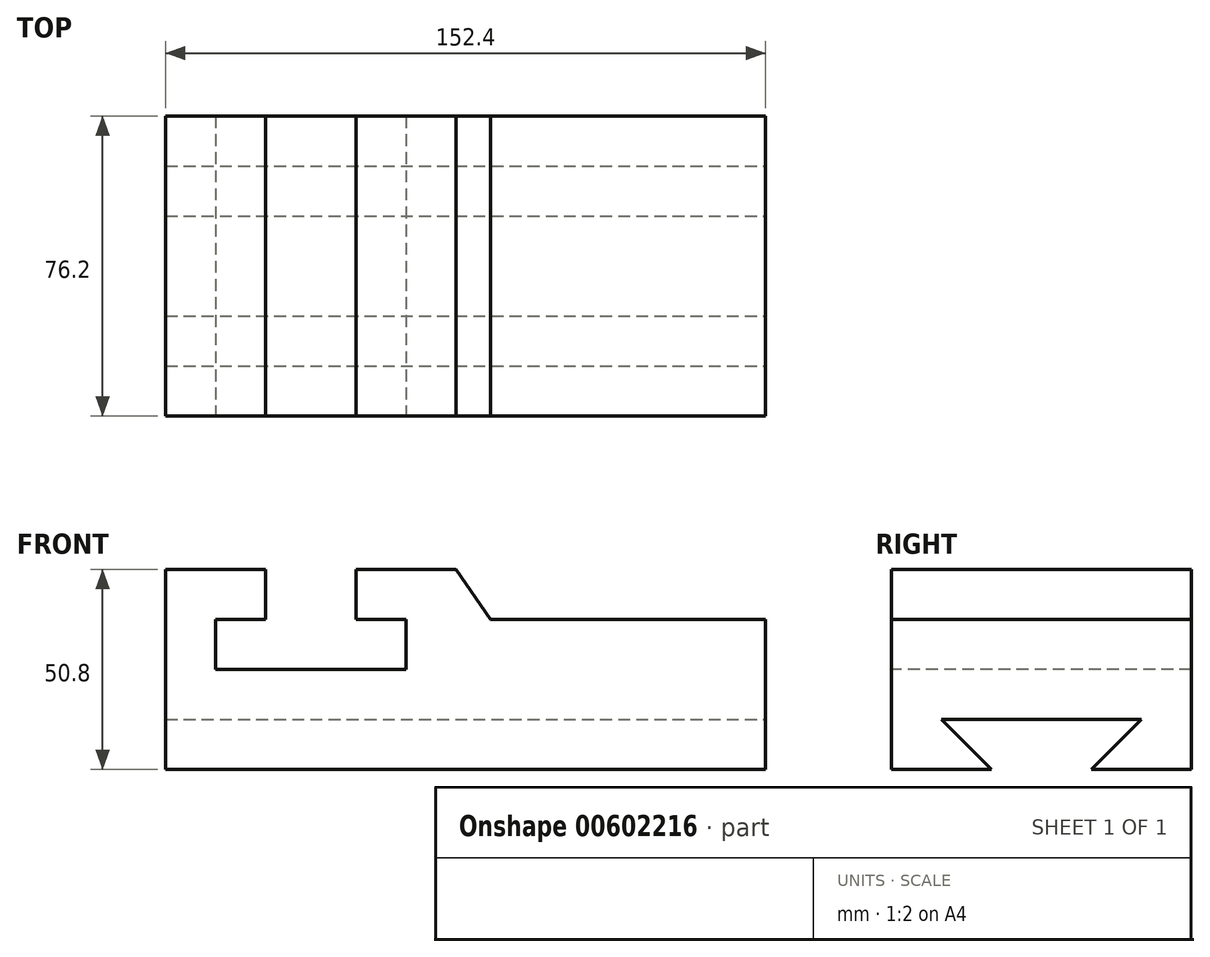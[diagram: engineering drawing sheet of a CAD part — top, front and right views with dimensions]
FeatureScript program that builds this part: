
annotation { "Feature Type Name" : "Feature", "Feature Type Description" : "" }
export const myFeature = defineFeature(function(context is Context, id is Id, definition is map)
    precondition{}
    {
        {
            var Q0;
            Q0=qCreatedBy(makeId("Front.planeOp"),FACE);
            var sketch = newSketch(context, id + "F0", { "sketchPlane" : qUnion([Q0])});
            skLineSegment(sketch, "E0.bottom", {"start": v(0, 0) * mm, "end": v(152.4, 0) * mm});
            skLineSegment(sketch, "E0.left", {"start": v(0, 0) * mm, "end": v(0, 50.8) * mm});
            skLineSegment(sketch, "E0.right", {"start": v(152.4, 0) * mm, "end": v(152.4, 38.1) * mm});
            skLineSegment(sketch, "E1", {"start": v(0, 50.8) * mm, "end": v(25.4, 50.8) * mm});
            skLineSegment(sketch, "E2", {"start": v(25.4, 50.8) * mm, "end": v(25.4, 38.1) * mm});
            skLineSegment(sketch, "E3", {"start": v(25.4, 38.1) * mm, "end": v(12.7, 38.1) * mm});
            skLineSegment(sketch, "E4", {"start": v(12.7, 38.1) * mm, "end": v(12.7, 25.4) * mm});
            skLineSegment(sketch, "E5", {"start": v(12.7, 25.4) * mm, "end": v(61.04, 25.4) * mm});
            skLineSegment(sketch, "E6", {"start": v(61.04, 25.4) * mm, "end": v(61.04, 38.1) * mm});
            skLineSegment(sketch, "E7", {"start": v(61.04, 38.1) * mm, "end": v(48.34, 38.1) * mm});
            skLineSegment(sketch, "E8", {"start": v(48.34, 38.1) * mm, "end": v(48.34, 50.8) * mm});
            skLineSegment(sketch, "E9", {"start": v(48.34, 50.8) * mm, "end": v(73.74, 50.8) * mm});
            skLineSegment(sketch, "E10", {"start": v(152.4, 38.1) * mm, "end": v(82.55, 38.1) * mm});
            skLineSegment(sketch, "E11", {"start": v(73.74, 50.8) * mm, "end": v(82.55, 38.1) * mm});
            skSolve(sketch);
        }
        {
            var Q0;
            Q0=makeQuery(id+"F0.imprint","IMPRINT",FACE,{"disambiguationData":[TD([[makeQuery(id+"F0.imprint","IMPRINT",EDGE,{"derivedFrom":sQuery(id+"F0.wireOp",EDGE,"E0.bottom")}),1.0]])]});
            extrude(context, id + "F1", {"entities" : qUnion([Q0]), "oppositeDirection" : true, "depth" : 76.2 * mm, "offsetDistance" : 25.4 * mm});
        }
        {
            var Q0;
            Q0=makeQuery(id+"F1.opExtrude","SWEPT_FACE",FACE,{"disambiguationData":[OSD([sQuery(id+"F0.wireOp",EDGE,"E0.right")])]});
            var sketch = newSketch(context, id + "F2", { "sketchPlane" : qUnion([Q0])});
            skLineSegment(sketch, "E12", {"start": v(0, 0) * mm, "end": v(25.4, 0) * mm});
            skLineSegment(sketch, "E13", {"start": v(76.2, 0) * mm, "end": v(50.8, 0) * mm});
            skLineSegment(sketch, "E14", {"start": v(25.4, 0) * mm, "end": v(12.7, 12.7) * mm});
            skLineSegment(sketch, "E15", {"start": v(50.8, 0) * mm, "end": v(63.5, 12.7) * mm});
            skLineSegment(sketch, "E16", {"start": v(12.7, 12.7) * mm, "end": v(63.5, 12.7) * mm});
            skSolve(sketch);
        }
        {
            var Q0;
            {var subQ0=sQuery(id+"F2.wireOp",EDGE,"E14");Q0=makeQuery(id+"F2.imprint","IMPRINT",FACE,{"disambiguationData":[TD([[makeQuery(id+"F2.imprint","IMPRINT",EDGE,{"derivedFrom":subQ0}),-1.0]])]});}
            extrude(context, id + "F3", {"entities" : qUnion([Q0]), "operationType" : NewBodyOperationType.REMOVE, "oppositeDirection" : true, "depth" : 152.4 * mm, "offsetDistance" : 25.4 * mm});
        }
    });
